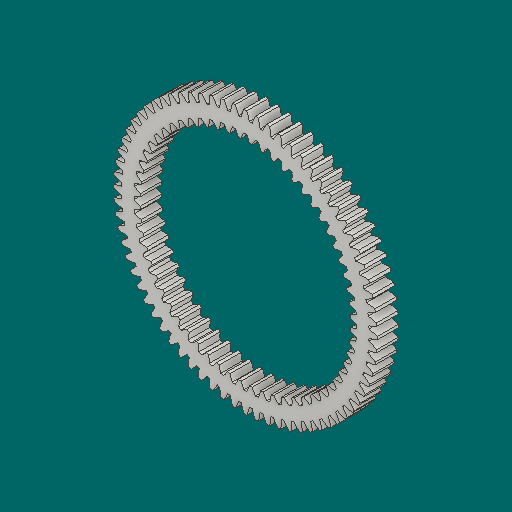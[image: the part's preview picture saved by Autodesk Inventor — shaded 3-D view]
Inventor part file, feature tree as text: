
AUTODESK INVENTOR PART (.ipt)
format: ipt  version: 2023.1 (Build 271208000, 208)  size: 933,888 bytes
history: native  units: in
note: dims shown in document units (in); Inventor stores cm internally (conversion verified against a paired STEP export)
features: other x12, sketch x3, plane x3
ambient origin geometry x8: Origin, YZ Plane, XZ Plane, XY Plane, X Axis, Y Axis, Z Axis, Center Point
bodies: Solid1_1 (feature_tree)
feature tree (18):
  other  "Spur Gear12_MIR.ipt"
  other  "Solid1_1::Spur Gear12_MIR.ipt"
  other  "TaggingFeature1"
  sketch  "Sketch1"  dims[d0=0.3937in]
  sketch  "Sketch2"  dims[d9=0.0in]
  sketch  "Sketch3"  dims[d14=0.0in d15=3.6in d16=0.0in d17=0.0in d18=0.0in d19=3.6in]
  plane  "XZ Plane_1"
  plane  "Work Plane2"
  plane  "Work Plane3"
  other  "Srf1"
  other  "Srf1::Derived"
  other  "Start plane iMate"
  other  "Distance iMate"
  other  "Position iMate"
  other  "Mesh iMate"
  other  "Axis iMate"
  other  "Mesh iMate2"
  other  "Align iMate"
